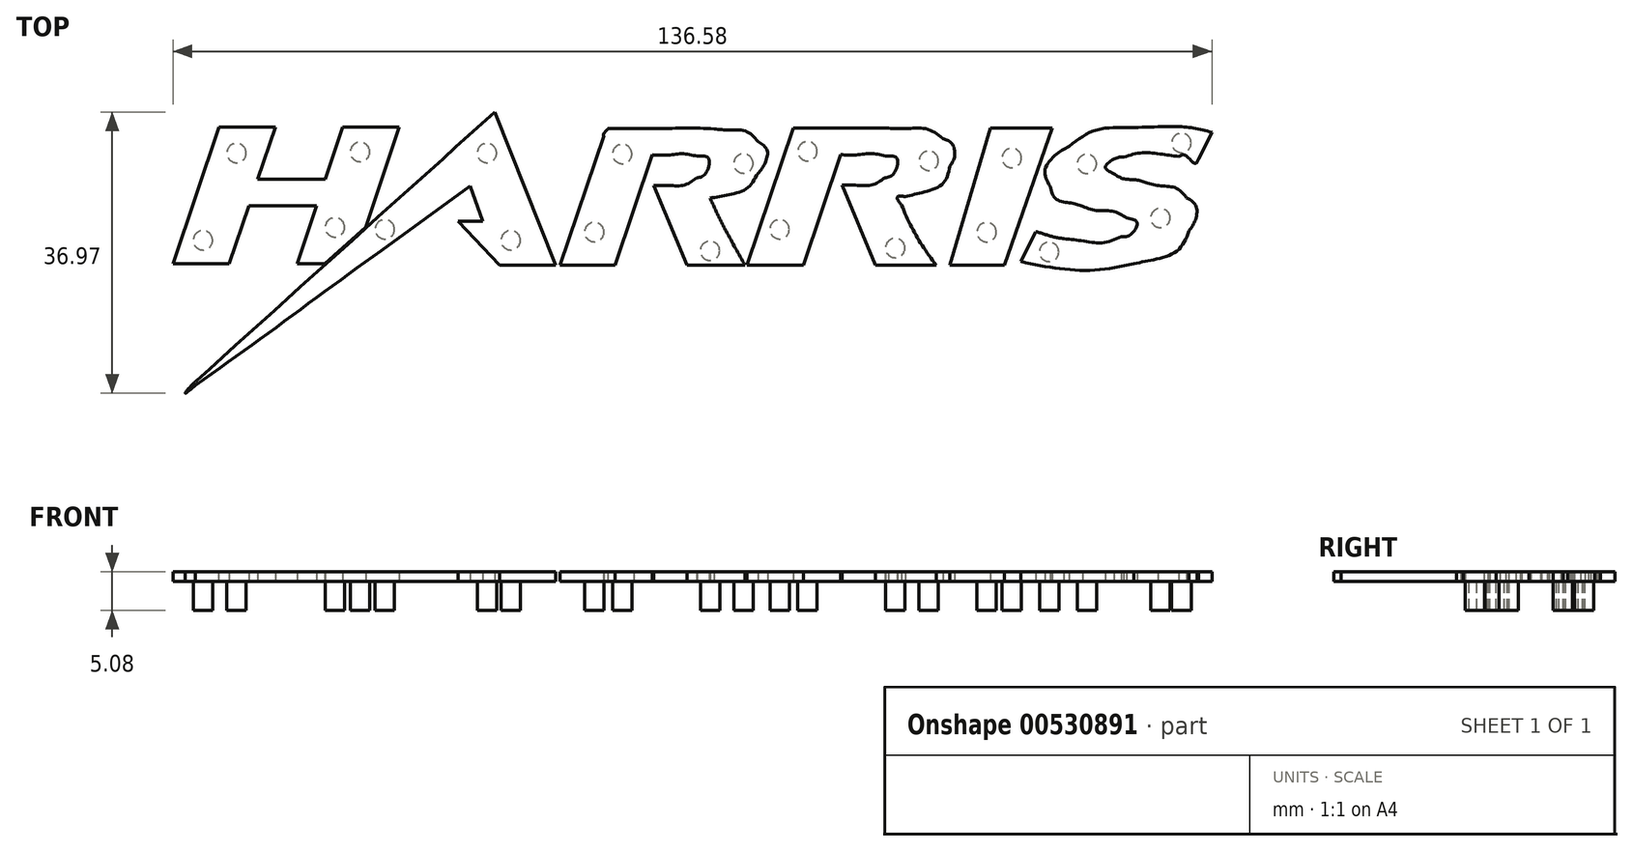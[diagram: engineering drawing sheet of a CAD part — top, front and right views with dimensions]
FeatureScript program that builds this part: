
annotation { "Feature Type Name" : "Feature", "Feature Type Description" : "" }
export const myFeature = defineFeature(function(context is Context, id is Id, definition is map)
    precondition{}
    {
        {
            var Q0;
            Q0=qCreatedBy(makeId("Top.planeOp"),FACE);
            var sketch = newSketch(context, id + "F0", { "sketchPlane" : qUnion([Q0])});
            skFitSpline(sketch, "E0", {"points": [v(64.98, 11.84) * mm, v(60.98, 11.74) * mm, v(56.78, 11.39) * mm, v(53.28, 9.28) * mm]});
            skFitSpline(sketch, "E1", {"points": [v(53.28, 9.28) * mm, v(51.58, 8.2) * mm, v(50.1, 6.06) * mm, v(50.81, 3.99) * mm]});
            skFitSpline(sketch, "E2", {"points": [v(50.81, 3.99) * mm, v(51.56, 2.34) * mm, v(53.47, 1.81) * mm, v(55.08, 1.37) * mm]});
            skFitSpline(sketch, "E3", {"points": [v(55.08, 1.37) * mm, v(57, 0.81) * mm, v(59.06, 0.72) * mm, v(60.88, -0.15) * mm]});
            skFitSpline(sketch, "E4", {"points": [v(60.88, -0.15) * mm, v(62.24, -0.8) * mm, v(61.28, -2.42) * mm, v(60.14, -2.63) * mm]});
            skFitSpline(sketch, "E5", {"points": [v(60.14, -2.63) * mm, v(57.72, -3.42) * mm, v(55.1, -3.18) * mm, v(52.61, -2.88) * mm]});
            skFitSpline(sketch, "E6", {"points": [v(52.61, -2.88) * mm, v(51.37, -2.67) * mm, v(50.15, -2.32) * mm, v(48.94, -1.95) * mm]});
            skFitSpline(sketch, "E7", {"points": [v(48.94, -1.95) * mm, v(48.28, -3.26) * mm, v(47.62, -4.57) * mm, v(46.96, -5.88) * mm]});
            skFitSpline(sketch, "E8", {"points": [v(46.96, -5.88) * mm, v(51.85, -6.8) * mm, v(56.9, -6.99) * mm, v(61.8, -6.16) * mm]});
            skFitSpline(sketch, "E9", {"points": [v(61.8, -6.16) * mm, v(64.6, -5.6) * mm, v(67.56, -4.42) * mm, v(69.06, -1.85) * mm]});
            skFitSpline(sketch, "E10", {"points": [v(69.06, -1.85) * mm, v(69.85, -0.53) * mm, v(69.99, 1.4) * mm, v(68.74, 2.5) * mm]});
            skFitSpline(sketch, "E11", {"points": [v(68.74, 2.5) * mm, v(67.26, 3.8) * mm, v(65.21, 4.07) * mm, v(63.36, 4.53) * mm]});
            skFitSpline(sketch, "E12", {"points": [v(63.36, 4.53) * mm, v(61.97, 4.87) * mm, v(60.47, 5) * mm, v(59.18, 5.65) * mm]});
            skFitSpline(sketch, "E13", {"points": [v(59.18, 5.65) * mm, v(58.08, 6.55) * mm, v(59.5, 7.72) * mm, v(60.47, 7.85) * mm]});
            skFitSpline(sketch, "E14", {"points": [v(60.47, 7.85) * mm, v(62.84, 8.41) * mm, v(65.32, 8.24) * mm, v(67.72, 7.94) * mm]});
            skFitSpline(sketch, "E15", {"points": [v(67.72, 7.94) * mm, v(68.54, 8.1) * mm, v(69.83, 7) * mm, v(70.34, 7.6) * mm]});
            skFitSpline(sketch, "E16", {"points": [v(70.34, 7.6) * mm, v(70.91, 8.77) * mm, v(71.48, 9.94) * mm, v(72.06, 11.1) * mm]});
            skFitSpline(sketch, "E17", {"points": [v(72.06, 11.1) * mm, v(69.75, 11.67) * mm, v(67.34, 11.85) * mm, v(64.98, 11.84) * mm]});
            skLineSegment(sketch, "E18", {"start": v(-58.49, 11.82) * mm, "end": v(-64.52, -6.17) * mm});
            skLineSegment(sketch, "E19", {"start": v(-64.52, -6.17) * mm, "end": v(-57.12, -6.17) * mm});
            skLineSegment(sketch, "E20", {"start": v(-57.12, -6.17) * mm, "end": v(-54.56, 1.45) * mm});
            skLineSegment(sketch, "E21", {"start": v(-54.56, 1.45) * mm, "end": v(-45.65, 1.45) * mm});
            skLineSegment(sketch, "E22", {"start": v(-45.65, 1.45) * mm, "end": v(-48.21, -6.17) * mm});
            skLineSegment(sketch, "E23", {"start": v(-48.21, -6.17) * mm, "end": v(-44.55, -6.17) * mm});
            skLineSegment(sketch, "E24", {"start": v(-44.55, -6.17) * mm, "end": v(-39.18, -1.34) * mm});
            skLineSegment(sketch, "E25", {"start": v(-39.18, -1.34) * mm, "end": v(-34.79, 11.82) * mm});
            skLineSegment(sketch, "E26", {"start": v(-34.79, 11.82) * mm, "end": v(-42.18, 11.82) * mm});
            skLineSegment(sketch, "E27", {"start": v(-42.18, 11.82) * mm, "end": v(-44.5, 4.91) * mm});
            skLineSegment(sketch, "E28", {"start": v(-44.5, 4.91) * mm, "end": v(-53.39, 4.91) * mm});
            skLineSegment(sketch, "E29", {"start": v(-53.39, 4.91) * mm, "end": v(-51.07, 11.82) * mm});
            skLineSegment(sketch, "E30", {"start": v(-51.07, 11.82) * mm, "end": v(-58.49, 11.82) * mm});
            skLineSegment(sketch, "E31", {"start": v(-152.3, 2.04) * mm, "end": v(-152.3, 2.04) * mm});
            skFitSpline(sketch, "E32", {"points": [v(8.2, -1.88) * mm, v(7.45, -0.47) * mm, v(6.76, 0.99) * mm, v(6.08, 2.44) * mm]});
            skFitSpline(sketch, "E33", {"points": [v(6.08, 2.44) * mm, v(8.4, 2.88) * mm, v(10.9, 3.74) * mm, v(12.37, 5.72) * mm]});
            skFitSpline(sketch, "E34", {"points": [v(12.37, 5.72) * mm, v(13.24, 6.9) * mm, v(13.58, 8.77) * mm, v(12.4, 9.88) * mm]});
            skFitSpline(sketch, "E35", {"points": [v(12.4, 9.88) * mm, v(10.8, 11.24) * mm, v(8.6, 11.4) * mm, v(6.6, 11.57) * mm]});
            skFitSpline(sketch, "E36", {"points": [v(6.6, 11.57) * mm, v(3.09, 11.67) * mm, v(-0.43, 11.6) * mm, v(-3.95, 11.62) * mm]});
            skFitSpline(sketch, "E37", {"points": [v(-3.95, 11.62) * mm, v(-5.21, 11.62) * mm, v(-6.47, 11.62) * mm, v(-7.74, 11.62) * mm]});
            skFitSpline(sketch, "E38", {"points": [v(-7.74, 11.62) * mm, v(-7.36, 11.62) * mm, v(-7.88, 10.94) * mm, v(-7.9, 10.65) * mm]});
            skFitSpline(sketch, "E39", {"points": [v(-7.9, 10.65) * mm, v(-9.81, 4.98) * mm, v(-11.74, -0.7) * mm, v(-13.66, -6.36) * mm]});
            skFitSpline(sketch, "E40", {"points": [v(-13.66, -6.36) * mm, v(-11.23, -6.36) * mm, v(-8.8, -6.37) * mm, v(-6.37, -6.37) * mm]});
            skFitSpline(sketch, "E41", {"points": [v(-6.37, -6.37) * mm, v(-4.74, -1.53) * mm, v(-3.11, 3.31) * mm, v(-1.49, 8.15) * mm]});
            skFitSpline(sketch, "E42", {"points": [v(-1.49, 8.15) * mm, v(0.47, 8.1) * mm, v(2.46, 8.29) * mm, v(4.4, 7.96) * mm]});
            skFitSpline(sketch, "E43", {"points": [v(4.4, 7.96) * mm, v(5.91, 7.66) * mm, v(5.42, 5.6) * mm, v(4.3, 5.1) * mm]});
            skFitSpline(sketch, "E44", {"points": [v(4.3, 5.1) * mm, v(2.6, 4.16) * mm, v(0.58, 4.12) * mm, v(-1.32, 4.12) * mm]});
            skFitSpline(sketch, "E45", {"points": [v(-1.32, 4.12) * mm, v(0.15, 0.62) * mm, v(1.61, -2.87) * mm, v(3.08, -6.37) * mm]});
            skFitSpline(sketch, "E46", {"points": [v(3.08, -6.37) * mm, v(5.61, -6.38) * mm, v(8.15, -6.38) * mm, v(10.68, -6.39) * mm]});
            skFitSpline(sketch, "E47", {"points": [v(10.68, -6.39) * mm, v(9.85, -4.9) * mm, v(9.02, -3.39) * mm, v(8.2, -1.88) * mm]});
            skLineSegment(sketch, "E48", {"start": v(-77.74, -11.46) * mm, "end": v(-77.74, -11.46) * mm});
            skFitSpline(sketch, "E49", {"points": [v(18.37, -6.35) * mm, v(20, -1.5) * mm, v(21.63, 3.34) * mm, v(23.25, 8.18) * mm]});
            skFitSpline(sketch, "E50", {"points": [v(23.25, 8.18) * mm, v(25.21, 8.13) * mm, v(27.2, 8.31) * mm, v(29.14, 7.98) * mm]});
            skFitSpline(sketch, "E51", {"points": [v(29.14, 7.98) * mm, v(30.65, 7.69) * mm, v(30.2, 5.63) * mm, v(29.07, 5.13) * mm]});
            skFitSpline(sketch, "E52", {"points": [v(29.07, 5.13) * mm, v(27.37, 4.18) * mm, v(25.33, 4.15) * mm, v(23.43, 4.15) * mm]});
            skFitSpline(sketch, "E53", {"points": [v(23.43, 4.15) * mm, v(24.9, 0.65) * mm, v(26.35, -2.85) * mm, v(27.82, -6.35) * mm]});
            skFitSpline(sketch, "E54", {"points": [v(27.82, -6.35) * mm, v(30.49, -6.35) * mm, v(33.16, -6.35) * mm, v(35.83, -6.35) * mm]});
            skFitSpline(sketch, "E55", {"points": [v(35.83, -6.35) * mm, v(34.04, -3.88) * mm, v(32.5, -1.24) * mm, v(31.26, 1.53) * mm]});
            skFitSpline(sketch, "E56", {"points": [v(31.26, 1.53) * mm, v(30.75, 2.25) * mm, v(30.77, 2.67) * mm, v(31.74, 2.65) * mm]});
            skFitSpline(sketch, "E57", {"points": [v(31.74, 2.65) * mm, v(34.05, 3.22) * mm, v(36.65, 4.31) * mm, v(37.63, 6.68) * mm]});
            skFitSpline(sketch, "E58", {"points": [v(37.63, 6.68) * mm, v(38.22, 7.91) * mm, v(37.92, 9.57) * mm, v(36.69, 10.3) * mm]});
            skFitSpline(sketch, "E59", {"points": [v(36.69, 10.3) * mm, v(34.55, 11.55) * mm, v(31.97, 11.6) * mm, v(29.55, 11.64) * mm]});
            skFitSpline(sketch, "E60", {"points": [v(29.55, 11.64) * mm, v(25.37, 11.64) * mm, v(21.19, 11.64) * mm, v(17, 11.64) * mm]});
            skFitSpline(sketch, "E61", {"points": [v(17, 11.64) * mm, v(14.97, 5.64) * mm, v(12.94, -0.36) * mm, v(10.91, -6.36) * mm]});
            skFitSpline(sketch, "E62", {"points": [v(10.91, -6.36) * mm, v(13.4, -6.36) * mm, v(15.89, -6.35) * mm, v(18.37, -6.35) * mm]});
            skLineSegment(sketch, "E63", {"start": v(-64.93, -15.95) * mm, "end": v(-64.93, -15.95) * mm});
            skLineSegment(sketch, "E64", {"start": v(44.76, -6.35) * mm, "end": v(51.04, 11.64) * mm});
            skLineSegment(sketch, "E65", {"start": v(51.04, 11.64) * mm, "end": v(42.96, 11.64) * mm});
            skLineSegment(sketch, "E66", {"start": v(42.96, 11.64) * mm, "end": v(37.63, -6.35) * mm});
            skLineSegment(sketch, "E67", {"start": v(37.63, -6.35) * mm, "end": v(44.76, -6.35) * mm});
            skFitSpline(sketch, "E68", {"points": [v(-22.22, 13.78) * mm, v(-35.28, 2) * mm, v(-48.36, -9.76) * mm, v(-61.4, -21.55) * mm]});
            skFitSpline(sketch, "E69", {"points": [v(-61.4, -21.55) * mm, v(-62.1, -22.22) * mm, v(-62.92, -23.18) * mm, v(-61.58, -22.2) * mm]});
            skFitSpline(sketch, "E70", {"points": [v(-61.58, -22.2) * mm, v(-53.4, -16.35) * mm, v(-45.3, -10.37) * mm, v(-37.16, -4.47) * mm]});
            skFitSpline(sketch, "E71", {"points": [v(-37.16, -4.47) * mm, v(-33.26, -1.64) * mm, v(-29.37, 1.2) * mm, v(-25.47, 4.03) * mm]});
            skFitSpline(sketch, "E72", {"points": [v(-25.47, 4.03) * mm, v(-24.91, 2.5) * mm, v(-24.35, 0.96) * mm, v(-23.8, -0.57) * mm]});
            skFitSpline(sketch, "E73", {"points": [v(-23.8, -0.57) * mm, v(-24.86, -0.57) * mm, v(-25.94, -0.57) * mm, v(-27.01, -0.57) * mm]});
            skFitSpline(sketch, "E74", {"points": [v(-27.01, -0.57) * mm, v(-25.2, -2.5) * mm, v(-23.4, -4.43) * mm, v(-21.6, -6.36) * mm]});
            skFitSpline(sketch, "E75", {"points": [v(-21.6, -6.36) * mm, v(-19.13, -6.36) * mm, v(-16.66, -6.36) * mm, v(-14.19, -6.36) * mm]});
            skFitSpline(sketch, "E76", {"points": [v(-14.19, -6.36) * mm, v(-16.87, 0.35) * mm, v(-19.54, 7.07) * mm, v(-22.22, 13.78) * mm]});
            skCircle(sketch, "E77", {"center": v(-56.17, 8.37) * mm, "radius": 1.27 * mm});
            skCircle(sketch, "E78", {"center": v(-60.57, -3.1) * mm, "radius": 1.27 * mm});
            skCircle(sketch, "E79", {"center": v(-39.93, 8.52) * mm, "radius": 1.27 * mm});
            skCircle(sketch, "E80", {"center": v(-43.23, -1.39) * mm, "radius": 1.27 * mm});
            skCircle(sketch, "E81", {"center": v(-5.46, 8.25) * mm, "radius": 1.27 * mm});
            skCircle(sketch, "E82", {"center": v(-9.12, -2.01) * mm, "radius": 1.27 * mm});
            skCircle(sketch, "E83", {"center": v(10.48, 7) * mm, "radius": 1.27 * mm});
            skCircle(sketch, "E84", {"center": v(6.08, -4.47) * mm, "radius": 1.27 * mm});
            skCircle(sketch, "E85", {"center": v(-23.25, 8.38) * mm, "radius": 1.27 * mm});
            skCircle(sketch, "E86", {"center": v(-20.1, -3.1) * mm, "radius": 1.27 * mm});
            skCircle(sketch, "E87", {"center": v(45.74, 7.73) * mm, "radius": 1.27 * mm});
            skCircle(sketch, "E88", {"center": v(-36.67, -1.65) * mm, "radius": 1.27 * mm});
            skCircle(sketch, "E89", {"center": v(18.9, 8.62) * mm, "radius": 1.27 * mm});
            skCircle(sketch, "E90", {"center": v(15.23, -1.65) * mm, "radius": 1.27 * mm});
            skCircle(sketch, "E91", {"center": v(34.83, 7.36) * mm, "radius": 1.27 * mm});
            skCircle(sketch, "E92", {"center": v(30.43, -4.11) * mm, "radius": 1.27 * mm});
            skCircle(sketch, "E93", {"center": v(55.62, 6.95) * mm, "radius": 1.27 * mm});
            skCircle(sketch, "E94", {"center": v(50.66, -4.62) * mm, "radius": 1.27 * mm});
            skCircle(sketch, "E95", {"center": v(68.06, 9.7) * mm, "radius": 1.27 * mm});
            skCircle(sketch, "E96", {"center": v(65.3, -0.16) * mm, "radius": 1.27 * mm});
            skCircle(sketch, "E97", {"center": v(42.45, -2.02) * mm, "radius": 1.27 * mm});
            skSolve(sketch);
        }
        {
            var Q0;
            Q0=makeQuery(id+"F0.imprint","IMPRINT",FACE,{"disambiguationData":[TD([[makeQuery(id+"F0.imprint","IMPRINT",EDGE,{"derivedFrom":sQuery(id+"F0.wireOp",EDGE,"E32")}),1.0]])]});
            var Q1;
            Q1=makeQuery(id+"F0.imprint","IMPRINT",FACE,{"disambiguationData":[TD([[makeQuery(id+"F0.imprint","IMPRINT",EDGE,{"derivedFrom":sQuery(id+"F0.wireOp",EDGE,"E18")}),1.0]])]});
            var Q2;
            Q2=makeQuery(id+"F0.imprint","IMPRINT",FACE,{"disambiguationData":[TD([[makeQuery(id+"F0.imprint","IMPRINT",EDGE,{"derivedFrom":sQuery(id+"F0.wireOp",EDGE,"E0")}),1.0]])]});
            var Q3;
            Q3=makeQuery(id+"F0.imprint","IMPRINT",FACE,{"disambiguationData":[TD([[makeQuery(id+"F0.imprint","IMPRINT",EDGE,{"derivedFrom":sQuery(id+"F0.wireOp",EDGE,"E68")}),1.0]])]});
            var Q4;
            Q4=makeQuery(id+"F0.imprint","IMPRINT",FACE,{"disambiguationData":[TD([[makeQuery(id+"F0.imprint","IMPRINT",EDGE,{"derivedFrom":sQuery(id+"F0.wireOp",EDGE,"E64")}),1.0]])]});
            var Q5;
            Q5=makeQuery(id+"F0.imprint","IMPRINT",FACE,{"disambiguationData":[TD([[makeQuery(id+"F0.imprint","IMPRINT",EDGE,{"derivedFrom":sQuery(id+"F0.wireOp",EDGE,"E49")}),1.0]])]});
            var Q6;
            Q6=makeQuery(id+"F0.imprint","IMPRINT",FACE,{"disambiguationData":[TD([[makeQuery(id+"F0.imprint","IMPRINT",EDGE,{"derivedFrom":sQuery(id+"F0.wireOp",EDGE,"E95")}),1.0]])]});
            var Q7;
            Q7=makeQuery(id+"F0.imprint","IMPRINT",FACE,{"disambiguationData":[TD([[makeQuery(id+"F0.imprint","IMPRINT",EDGE,{"derivedFrom":sQuery(id+"F0.wireOp",EDGE,"E94")}),1.0]])]});
            var Q8;
            Q8=makeQuery(id+"F0.imprint","IMPRINT",FACE,{"disambiguationData":[TD([[makeQuery(id+"F0.imprint","IMPRINT",EDGE,{"derivedFrom":sQuery(id+"F0.wireOp",EDGE,"E89")}),1.0]])]});
            var Q9;
            Q9=makeQuery(id+"F0.imprint","IMPRINT",FACE,{"disambiguationData":[TD([[makeQuery(id+"F0.imprint","IMPRINT",EDGE,{"derivedFrom":sQuery(id+"F0.wireOp",EDGE,"E88")}),1.0]])]});
            var Q10;
            Q10=makeQuery(id+"F0.imprint","IMPRINT",FACE,{"disambiguationData":[TD([[makeQuery(id+"F0.imprint","IMPRINT",EDGE,{"derivedFrom":sQuery(id+"F0.wireOp",EDGE,"E86")}),1.0]])]});
            var Q11;
            Q11=makeQuery(id+"F0.imprint","IMPRINT",FACE,{"disambiguationData":[TD([[makeQuery(id+"F0.imprint","IMPRINT",EDGE,{"derivedFrom":sQuery(id+"F0.wireOp",EDGE,"E87")}),1.0]])]});
            var Q12;
            Q12=makeQuery(id+"F0.imprint","IMPRINT",FACE,{"disambiguationData":[TD([[makeQuery(id+"F0.imprint","IMPRINT",EDGE,{"derivedFrom":sQuery(id+"F0.wireOp",EDGE,"E84")}),1.0]])]});
            var Q13;
            Q13=makeQuery(id+"F0.imprint","IMPRINT",FACE,{"disambiguationData":[TD([[makeQuery(id+"F0.imprint","IMPRINT",EDGE,{"derivedFrom":sQuery(id+"F0.wireOp",EDGE,"E85")}),1.0]])]});
            var Q14;
            Q14=makeQuery(id+"F0.imprint","IMPRINT",FACE,{"disambiguationData":[TD([[makeQuery(id+"F0.imprint","IMPRINT",EDGE,{"derivedFrom":sQuery(id+"F0.wireOp",EDGE,"E83")}),1.0]])]});
            var Q15;
            Q15=makeQuery(id+"F0.imprint","IMPRINT",FACE,{"disambiguationData":[TD([[makeQuery(id+"F0.imprint","IMPRINT",EDGE,{"derivedFrom":sQuery(id+"F0.wireOp",EDGE,"E82")}),1.0]])]});
            var Q16;
            Q16=makeQuery(id+"F0.imprint","IMPRINT",FACE,{"disambiguationData":[TD([[makeQuery(id+"F0.imprint","IMPRINT",EDGE,{"derivedFrom":sQuery(id+"F0.wireOp",EDGE,"E81")}),1.0]])]});
            var Q17;
            Q17=makeQuery(id+"F0.imprint","IMPRINT",FACE,{"disambiguationData":[TD([[makeQuery(id+"F0.imprint","IMPRINT",EDGE,{"derivedFrom":sQuery(id+"F0.wireOp",EDGE,"E80")}),1.0]])]});
            var Q18;
            Q18=makeQuery(id+"F0.imprint","IMPRINT",FACE,{"disambiguationData":[TD([[makeQuery(id+"F0.imprint","IMPRINT",EDGE,{"derivedFrom":sQuery(id+"F0.wireOp",EDGE,"E79")}),1.0]])]});
            var Q19;
            Q19=makeQuery(id+"F0.imprint","IMPRINT",FACE,{"disambiguationData":[TD([[makeQuery(id+"F0.imprint","IMPRINT",EDGE,{"derivedFrom":sQuery(id+"F0.wireOp",EDGE,"E78")}),1.0]])]});
            var Q20;
            Q20=makeQuery(id+"F0.imprint","IMPRINT",FACE,{"disambiguationData":[TD([[makeQuery(id+"F0.imprint","IMPRINT",EDGE,{"derivedFrom":sQuery(id+"F0.wireOp",EDGE,"E77")}),1.0]])]});
            var Q21;
            Q21=makeQuery(id+"F0.imprint","IMPRINT",FACE,{"disambiguationData":[TD([[makeQuery(id+"F0.imprint","IMPRINT",EDGE,{"derivedFrom":sQuery(id+"F0.wireOp",EDGE,"E93")}),1.0]])]});
            var Q22;
            Q22=makeQuery(id+"F0.imprint","IMPRINT",FACE,{"disambiguationData":[TD([[makeQuery(id+"F0.imprint","IMPRINT",EDGE,{"derivedFrom":sQuery(id+"F0.wireOp",EDGE,"E91")}),1.0]])]});
            var Q23;
            Q23=makeQuery(id+"F0.imprint","IMPRINT",FACE,{"disambiguationData":[TD([[makeQuery(id+"F0.imprint","IMPRINT",EDGE,{"derivedFrom":sQuery(id+"F0.wireOp",EDGE,"E90")}),1.0]])]});
            var Q24;
            Q24=makeQuery(id+"F0.imprint","IMPRINT",FACE,{"disambiguationData":[TD([[makeQuery(id+"F0.imprint","IMPRINT",EDGE,{"derivedFrom":sQuery(id+"F0.wireOp",EDGE,"E92")}),1.0]])]});
            var Q25;
            Q25=makeQuery(id+"F0.imprint","IMPRINT",FACE,{"disambiguationData":[TD([[makeQuery(id+"F0.imprint","IMPRINT",EDGE,{"derivedFrom":sQuery(id+"F0.wireOp",EDGE,"E97")}),1.0]])]});
            var Q26;
            Q26=makeQuery(id+"F0.imprint","IMPRINT",FACE,{"disambiguationData":[TD([[makeQuery(id+"F0.imprint","IMPRINT",EDGE,{"derivedFrom":sQuery(id+"F0.wireOp",EDGE,"E96")}),1.0]])]});
            extrude(context, id + "F1", {"entities" : qUnion([Q0, Q1, Q2, Q3, Q4, Q5, Q6, Q7, Q8, Q9, Q10, Q11, Q12, Q13, Q14, Q15, Q16, Q17, Q18, Q19, Q20, Q21, Q22, Q23, Q24, Q25, Q26]), "depth" : 1.27 * mm, "offsetDistance" : 25.4 * mm});
        }
        {
            var Q0;
            Q0=makeQuery(id+"F0.imprint","IMPRINT",FACE,{"disambiguationData":[TD([[makeQuery(id+"F0.imprint","IMPRINT",EDGE,{"derivedFrom":sQuery(id+"F0.wireOp",EDGE,"E78")}),1.0]])]});
            var Q1;
            Q1=makeQuery(id+"F0.imprint","IMPRINT",FACE,{"disambiguationData":[TD([[makeQuery(id+"F0.imprint","IMPRINT",EDGE,{"derivedFrom":sQuery(id+"F0.wireOp",EDGE,"E77")}),1.0]])]});
            var Q2;
            Q2=makeQuery(id+"F0.imprint","IMPRINT",FACE,{"disambiguationData":[TD([[makeQuery(id+"F0.imprint","IMPRINT",EDGE,{"derivedFrom":sQuery(id+"F0.wireOp",EDGE,"E79")}),1.0]])]});
            var Q3;
            Q3=makeQuery(id+"F0.imprint","IMPRINT",FACE,{"disambiguationData":[TD([[makeQuery(id+"F0.imprint","IMPRINT",EDGE,{"derivedFrom":sQuery(id+"F0.wireOp",EDGE,"E80")}),1.0]])]});
            var Q4;
            Q4=makeQuery(id+"F0.imprint","IMPRINT",FACE,{"disambiguationData":[TD([[makeQuery(id+"F0.imprint","IMPRINT",EDGE,{"derivedFrom":sQuery(id+"F0.wireOp",EDGE,"E88")}),1.0]])]});
            var Q5;
            Q5=makeQuery(id+"F0.imprint","IMPRINT",FACE,{"disambiguationData":[TD([[makeQuery(id+"F0.imprint","IMPRINT",EDGE,{"derivedFrom":sQuery(id+"F0.wireOp",EDGE,"E86")}),1.0]])]});
            var Q6;
            Q6=makeQuery(id+"F0.imprint","IMPRINT",FACE,{"disambiguationData":[TD([[makeQuery(id+"F0.imprint","IMPRINT",EDGE,{"derivedFrom":sQuery(id+"F0.wireOp",EDGE,"E85")}),1.0]])]});
            var Q7;
            Q7=makeQuery(id+"F0.imprint","IMPRINT",FACE,{"disambiguationData":[TD([[makeQuery(id+"F0.imprint","IMPRINT",EDGE,{"derivedFrom":sQuery(id+"F0.wireOp",EDGE,"E82")}),1.0]])]});
            var Q8;
            Q8=makeQuery(id+"F0.imprint","IMPRINT",FACE,{"disambiguationData":[TD([[makeQuery(id+"F0.imprint","IMPRINT",EDGE,{"derivedFrom":sQuery(id+"F0.wireOp",EDGE,"E81")}),1.0]])]});
            var Q9;
            Q9=makeQuery(id+"F0.imprint","IMPRINT",FACE,{"disambiguationData":[TD([[makeQuery(id+"F0.imprint","IMPRINT",EDGE,{"derivedFrom":sQuery(id+"F0.wireOp",EDGE,"E84")}),1.0]])]});
            var Q10;
            Q10=makeQuery(id+"F0.imprint","IMPRINT",FACE,{"disambiguationData":[TD([[makeQuery(id+"F0.imprint","IMPRINT",EDGE,{"derivedFrom":sQuery(id+"F0.wireOp",EDGE,"E83")}),1.0]])]});
            var Q11;
            Q11=makeQuery(id+"F0.imprint","IMPRINT",FACE,{"disambiguationData":[TD([[makeQuery(id+"F0.imprint","IMPRINT",EDGE,{"derivedFrom":sQuery(id+"F0.wireOp",EDGE,"E90")}),1.0]])]});
            var Q12;
            Q12=makeQuery(id+"F0.imprint","IMPRINT",FACE,{"disambiguationData":[TD([[makeQuery(id+"F0.imprint","IMPRINT",EDGE,{"derivedFrom":sQuery(id+"F0.wireOp",EDGE,"E89")}),1.0]])]});
            var Q13;
            Q13=makeQuery(id+"F0.imprint","IMPRINT",FACE,{"disambiguationData":[TD([[makeQuery(id+"F0.imprint","IMPRINT",EDGE,{"derivedFrom":sQuery(id+"F0.wireOp",EDGE,"E92")}),1.0]])]});
            var Q14;
            Q14=makeQuery(id+"F0.imprint","IMPRINT",FACE,{"disambiguationData":[TD([[makeQuery(id+"F0.imprint","IMPRINT",EDGE,{"derivedFrom":sQuery(id+"F0.wireOp",EDGE,"E91")}),1.0]])]});
            var Q15;
            Q15=makeQuery(id+"F0.imprint","IMPRINT",FACE,{"disambiguationData":[TD([[makeQuery(id+"F0.imprint","IMPRINT",EDGE,{"derivedFrom":sQuery(id+"F0.wireOp",EDGE,"E97")}),1.0]])]});
            var Q16;
            Q16=makeQuery(id+"F0.imprint","IMPRINT",FACE,{"disambiguationData":[TD([[makeQuery(id+"F0.imprint","IMPRINT",EDGE,{"derivedFrom":sQuery(id+"F0.wireOp",EDGE,"E87")}),1.0]])]});
            var Q17;
            Q17=makeQuery(id+"F0.imprint","IMPRINT",FACE,{"disambiguationData":[TD([[makeQuery(id+"F0.imprint","IMPRINT",EDGE,{"derivedFrom":sQuery(id+"F0.wireOp",EDGE,"E94")}),1.0]])]});
            var Q18;
            Q18=makeQuery(id+"F0.imprint","IMPRINT",FACE,{"disambiguationData":[TD([[makeQuery(id+"F0.imprint","IMPRINT",EDGE,{"derivedFrom":sQuery(id+"F0.wireOp",EDGE,"E96")}),1.0]])]});
            var Q19;
            Q19=makeQuery(id+"F0.imprint","IMPRINT",FACE,{"disambiguationData":[TD([[makeQuery(id+"F0.imprint","IMPRINT",EDGE,{"derivedFrom":sQuery(id+"F0.wireOp",EDGE,"E93")}),1.0]])]});
            var Q20;
            Q20=makeQuery(id+"F0.imprint","IMPRINT",FACE,{"disambiguationData":[TD([[makeQuery(id+"F0.imprint","IMPRINT",EDGE,{"derivedFrom":sQuery(id+"F0.wireOp",EDGE,"E95")}),1.0]])]});
            extrude(context, id + "F2", {"entities" : qUnion([Q0, Q1, Q2, Q3, Q4, Q5, Q6, Q7, Q8, Q9, Q10, Q11, Q12, Q13, Q14, Q15, Q16, Q17, Q18, Q19, Q20]), "operationType" : NewBodyOperationType.ADD, "oppositeDirection" : true, "depth" : 3.8 * mm, "offsetDistance" : 25.4 * mm});
        }
    });
